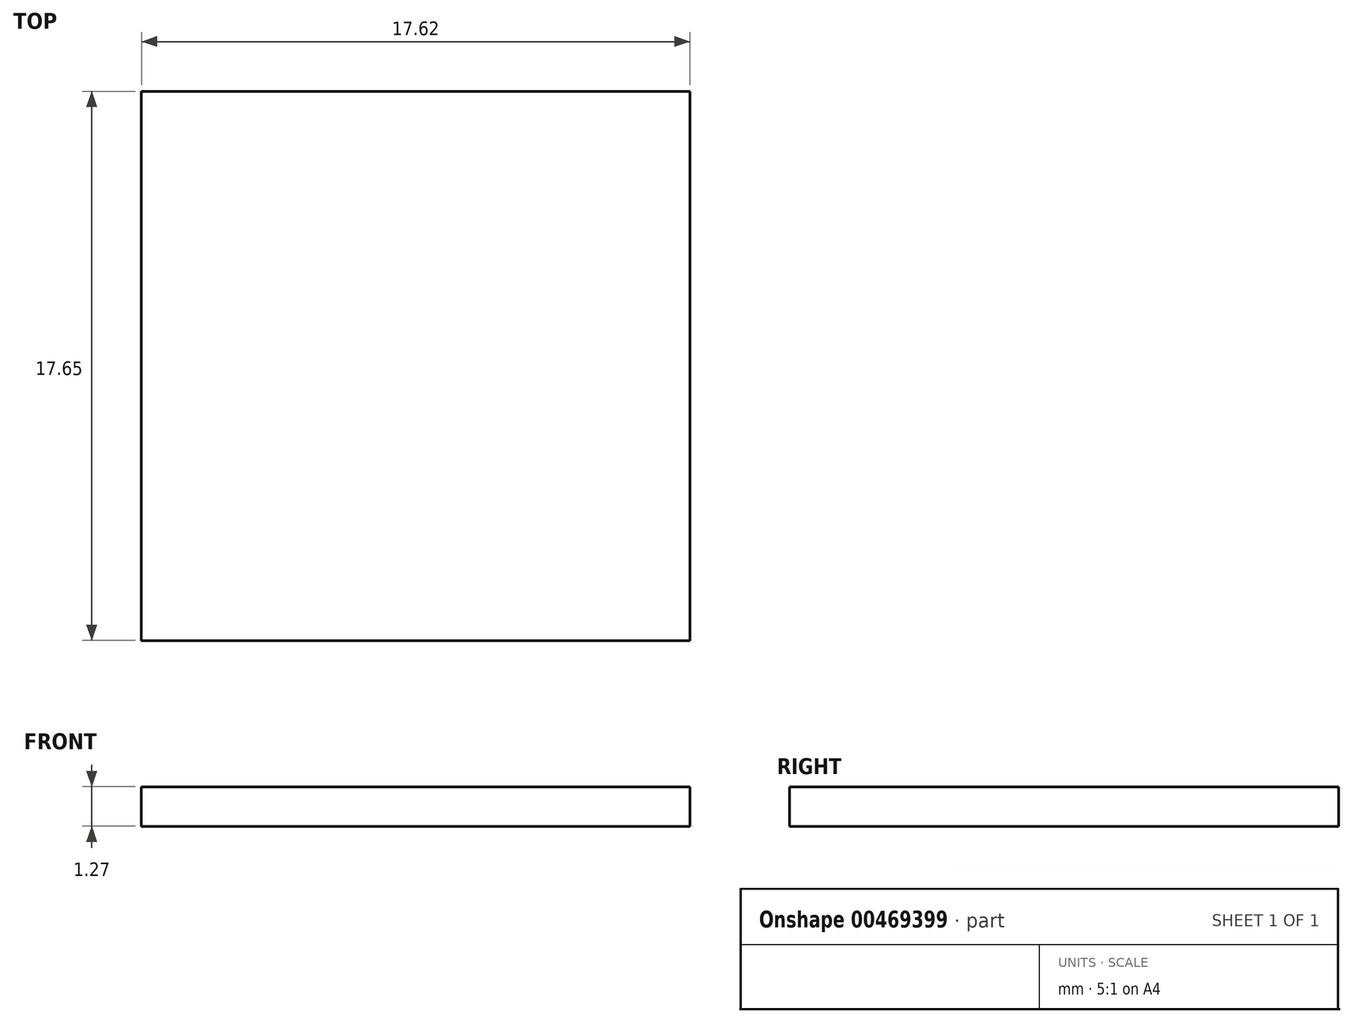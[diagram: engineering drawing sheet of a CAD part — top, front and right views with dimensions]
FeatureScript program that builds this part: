
annotation { "Feature Type Name" : "Feature", "Feature Type Description" : "" }
export const myFeature = defineFeature(function(context is Context, id is Id, definition is map)
    precondition{}
    {
        {
            var Q0;
            Q0=qCreatedBy(makeId("Top.planeOp"),FACE);
            var sketch = newSketch(context, id + "F0", { "sketchPlane" : qUnion([Q0])});
            skLineSegment(sketch, "E0.bottom", {"start": v(-76.03, 76.11) * mm, "end": v(0, 76.11) * mm});
            skLineSegment(sketch, "E0.top", {"start": v(-76.03, 0) * mm, "end": v(0, 0) * mm});
            skLineSegment(sketch, "E0.left", {"start": v(-76.03, 76.11) * mm, "end": v(-76.03, 0) * mm});
            skLineSegment(sketch, "E0.right", {"start": v(0, 76.11) * mm, "end": v(0, 0) * mm});
            skLineSegment(sketch, "E1", {"start": v(0, 0) * mm, "end": v(58.96, 0) * mm});
            skSolve(sketch);
        }
        {
            var Q0;
            Q0=makeQuery(id+"F0.imprint","IMPRINT",FACE,{"disambiguationData":[TD([[makeQuery(id+"F0.imprint","IMPRINT",EDGE,{"derivedFrom":sQuery(id+"F0.wireOp",EDGE,"E0.bottom")}),-1.0]])]});
            extrude(context, id + "F1", {"entities" : qUnion([Q0]), "depth" : 1.78 * mm});
        }
        {
            var Q0;
            Q0=makeQuery(id+"FHdNvDsw4lZGkoo_9.boolean.opBoolean","MERGE",FACE,{"derivedFrom":[makeQuery(id+"F1.opExtrude","CAP_FACE",FACE,{"disambiguationData":[OSD([sQuery(id+"F0.wireOp",EDGE,"E0.bottom"),sQuery(id+"F0.wireOp",EDGE,"E0.top"),sQuery(id+"F0.wireOp",EDGE,"E0.left"),sQuery(id+"F0.wireOp",EDGE,"E0.right")])],"isStart":false}),makeQuery(id+"FHdNvDsw4lZGkoo_9.opExtrude","SWEPT_FACE",FACE,{"disambiguationData":[OSD([sQuery(id+"FiOYn89Z3lF8DFt_9.wireOp",EDGE,"Rq5wyvzD-rGn9-TK9F-Gpxk-akdTn5OyZLWT.bottom")])]})]});
            var sketch = newSketch(context, id + "F2", { "sketchPlane" : qUnion([Q0])});
            skLineSegment(sketch, "E2.bottom", {"start": v(-66.7, -28.07) * mm, "end": v(-49.08, -28.07) * mm});
            skLineSegment(sketch, "E2.top", {"start": v(-66.7, -10.42) * mm, "end": v(-49.08, -10.42) * mm});
            skLineSegment(sketch, "E2.left", {"start": v(-66.7, -28.07) * mm, "end": v(-66.7, -10.42) * mm});
            skLineSegment(sketch, "E2.right", {"start": v(-49.08, -28.07) * mm, "end": v(-49.08, -10.42) * mm});
            skSolve(sketch);
        }
        {
            var Q0;
            Q0=makeQuery(id+"F2.imprint","IMPRINT",FACE,{"disambiguationData":[TD([[makeQuery(id+"F2.imprint","IMPRINT",EDGE,{"derivedFrom":sQuery(id+"F2.wireOp",EDGE,"E2.bottom")}),1.0]])]});
            extrude(context, id + "F3", {"entities" : qUnion([Q0]), "depth" : 1.27 * mm});
        }
        {
            var Q0;
            Q0=makeQuery(id+"F1.opExtrude","SWEPT_BODY",BODY,{"disambiguationData":[OSD([sQuery(id+"F0.wireOp",EDGE,"E0.bottom"),sQuery(id+"F0.wireOp",EDGE,"E0.top"),sQuery(id+"F0.wireOp",EDGE,"E0.left"),sQuery(id+"F0.wireOp",EDGE,"E0.right")])]});
            deleteBodies(context, id + "F4", {"entities" : qUnion([Q0])});
        }
    });
